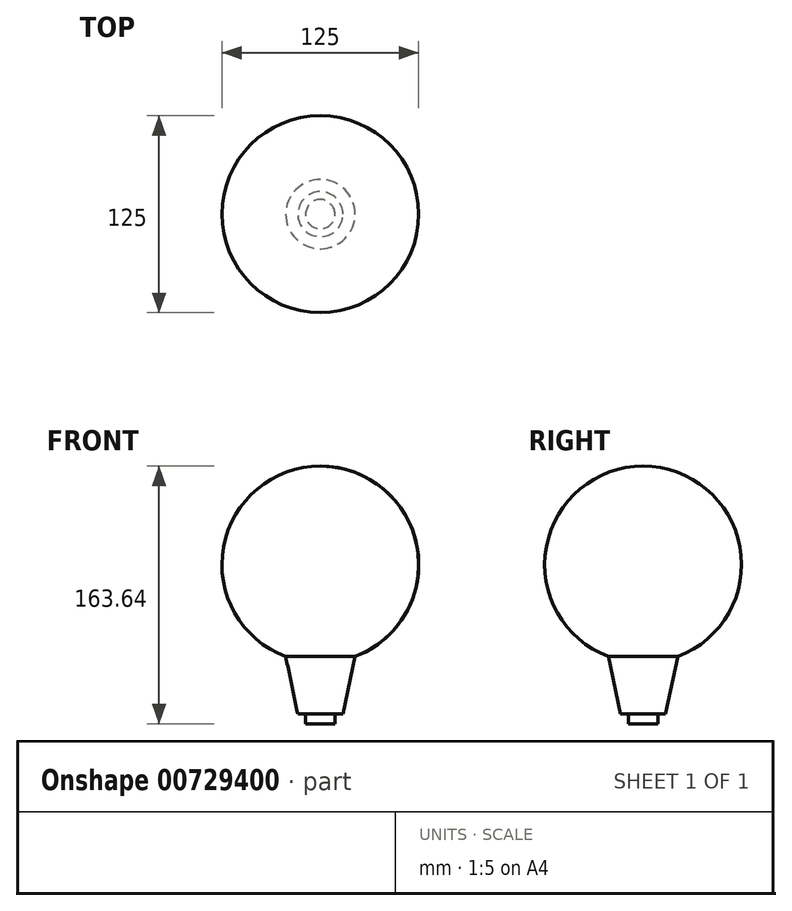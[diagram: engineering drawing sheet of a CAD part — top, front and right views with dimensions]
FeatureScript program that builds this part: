
annotation { "Feature Type Name" : "Feature", "Feature Type Description" : "" }
export const myFeature = defineFeature(function(context is Context, id is Id, definition is map)
    precondition{}
    {
        {
            var Q0;
            Q0=qCreatedBy(makeId("Front.planeOp"),FACE);
            var sketch = newSketch(context, id + "F0", { "sketchPlane" : qUnion([Q0])});
            skLineSegment(sketch, "E0", {"start": v(0, 0) * mm, "end": v(0, 125) * mm});
            skArc(sketch, "E1", {"start": v(0, 125) * mm, "mid": v(-61.49, 73.7) * mm, "end": v(-22.02, 4) * mm});
            skLineSegment(sketch, "E2", {"start": v(-22.02, 4) * mm, "end": v(-14.33, -32.54) * mm});
            skLineSegment(sketch, "E3", {"start": v(-14.33, -32.54) * mm, "end": v(0, -32.54) * mm});
            skLineSegment(sketch, "E4", {"start": v(0, -32.54) * mm, "end": v(0, 0) * mm});
            skSolve(sketch);
        }
        {
            var Q0;
            Q0=makeQuery(id+"F0.imprint","IMPRINT",FACE,{"disambiguationData":[TD([[makeQuery(id+"F0.imprint","IMPRINT",EDGE,{"derivedFrom":sQuery(id+"F0.wireOp",EDGE,"E0")}),1.0]])]});
            var Q1;
            Q1=sQuery(id+"F0.wireOp",EDGE,"E0");
            revolve(context, id + "F1", {"surfaceOperationType" : NewSurfaceOperationType.NEW, "entities" : qUnion([Q0]), "axis" : qUnion([Q1]), "revolveType" : RevolveType.FULL});
        }
        {
            var Q0;
            Q0=makeQuery(id+"F1.opRevolve","SWEPT_FACE",FACE,{"disambiguationData":[OSD([sQuery(id+"F0.wireOp",EDGE,"E3")])]});
            var sketch = newSketch(context, id + "F2", { "sketchPlane" : qUnion([Q0])});
            skCircle(sketch, "E5.0", {"center": v(0, 0) * mm, "radius": 9.33 * mm});
            skSolve(sketch);
        }
        {
            var Q0;
            Q0=makeQuery(id+"F2.imprint","IMPRINT",FACE,{"disambiguationData":[TD([[makeQuery(id+"F2.imprint","IMPRINT",EDGE,{"derivedFrom":sQuery(id+"F2.wireOp",EDGE,"E5.0")}),1.0]])]});
            extrude(context, id + "F3", {"entities" : qUnion([Q0]), "operationType" : NewBodyOperationType.ADD, "depth" : 6.1 * mm, "offsetDistance" : 25 * mm});
        }
    });
